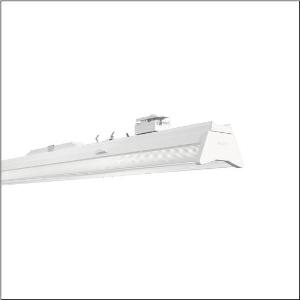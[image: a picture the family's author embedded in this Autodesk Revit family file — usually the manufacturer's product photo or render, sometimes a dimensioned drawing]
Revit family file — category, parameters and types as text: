
# Revit family: licross_r__21_performance_mo_52tm16dn46xg_f566
name_source: partatom
category: Lighting Fixtures
units: mm (PartAtom-declared; Revit-internal decimal feet)

## family parameters
Cut with Voids When Loaded = No
Host = Face
Light Source = No
Part Type = Normal
Room Calculation Point = No
Round Connector Dimension = Use Diameter
Shared = No

## types (1)
- --- (1 x LED, 6000 lm, 32.7 W, 4000K)
    Apparent Load = 33 VA
    CIE Flux Codes = 66 88 96 79 100
    Color Rendering = 80
    Color Temperature = 4000K
    Default Elevation = 1800 mm
    Description = Licross® 21 Performance MO, luminaire insert, of sheet steel, galvanised, coil coated, white, length: 1.500mm, width: 120mm, height: 123mm, LED rated luminous flux: 6.000lm, light colour: 840, control gear: DALI 2, with plug, 5-pole, with phase selection, mains connection: 220..240V, AC, 50/60Hz, rated input power: 33W, halogen-free wiring, primary light control with lens, of plastic, primary optical cover: cover, of PMMA, light emission: direct/indirect distribution, primary light characteristic: symmetric, protection rating (complete): IP40, insulation class (complete): insulation class I (protective earthing), certification: CE, ENEC, UKCA, protection symbol: D if used in an environment without relevant dust loads with corresponding accessories, impact resistance: IK06, permissible ambient temperature for indoor applications: -25..+45°C, corresponds to IFS (International Featured Standards) requirements for safety and quality in the food industry, reducing of maximum allowable ambient temperature of 5°C with ceiling mounting, LABS conformity tested according to VDMA 24364:2018-05, packaging unit: 1 piece
    Height = 114 mm
    Lamp = 1 x LED
    Lamp Light Flux = 6000 lm
    Lamp Power = 32.7 W
    Lamp count = 1
    Length = 1500 mm
    Luminous efficacy = 183 lm/W
    Manufacturer = Siteco
    ModVariant = No
    Model = 52TM16DN46XG
    Mounting Place = Ceiling
    Mounting Type = Pendant
    Number of Poles = 1
    OnlyDefault = Yes
    Power Factor = 1
    Product Name = Licross® 21 Performance MO
    Product group = luminaire insert
    ProductGroupID = 901
    Protection Class = Protection class I
    Protection Degree = IP 40
    RLX_Detail_Level = 1
    RLX_Emergency_Light_Flux = 0 lm
    RLX_Emergency_Type = 0
    RLX_Emergency_Type_DB = No
    RlxData = <blob elided: 33713 chars, md5=994c351a>
    Socket = socket
    Standby Power = 0 W
    System Light Flux = 6000 lm
    System Power = 33 W
    Type Comments = factory setting: luminous flux: 100 % | dim-lin: 254 | 222 mA
    Type Image = l_1256138.jpg
    URL = http://relux.com
    VarID = @adj_078961
    Voltage = 0 V
    Weight = 0.00 kg
    Width = 120 mm

## geometry (parser evidence)
native form markers: Blend x4, Sweep x13
no freeform markers — native parametric forms only
